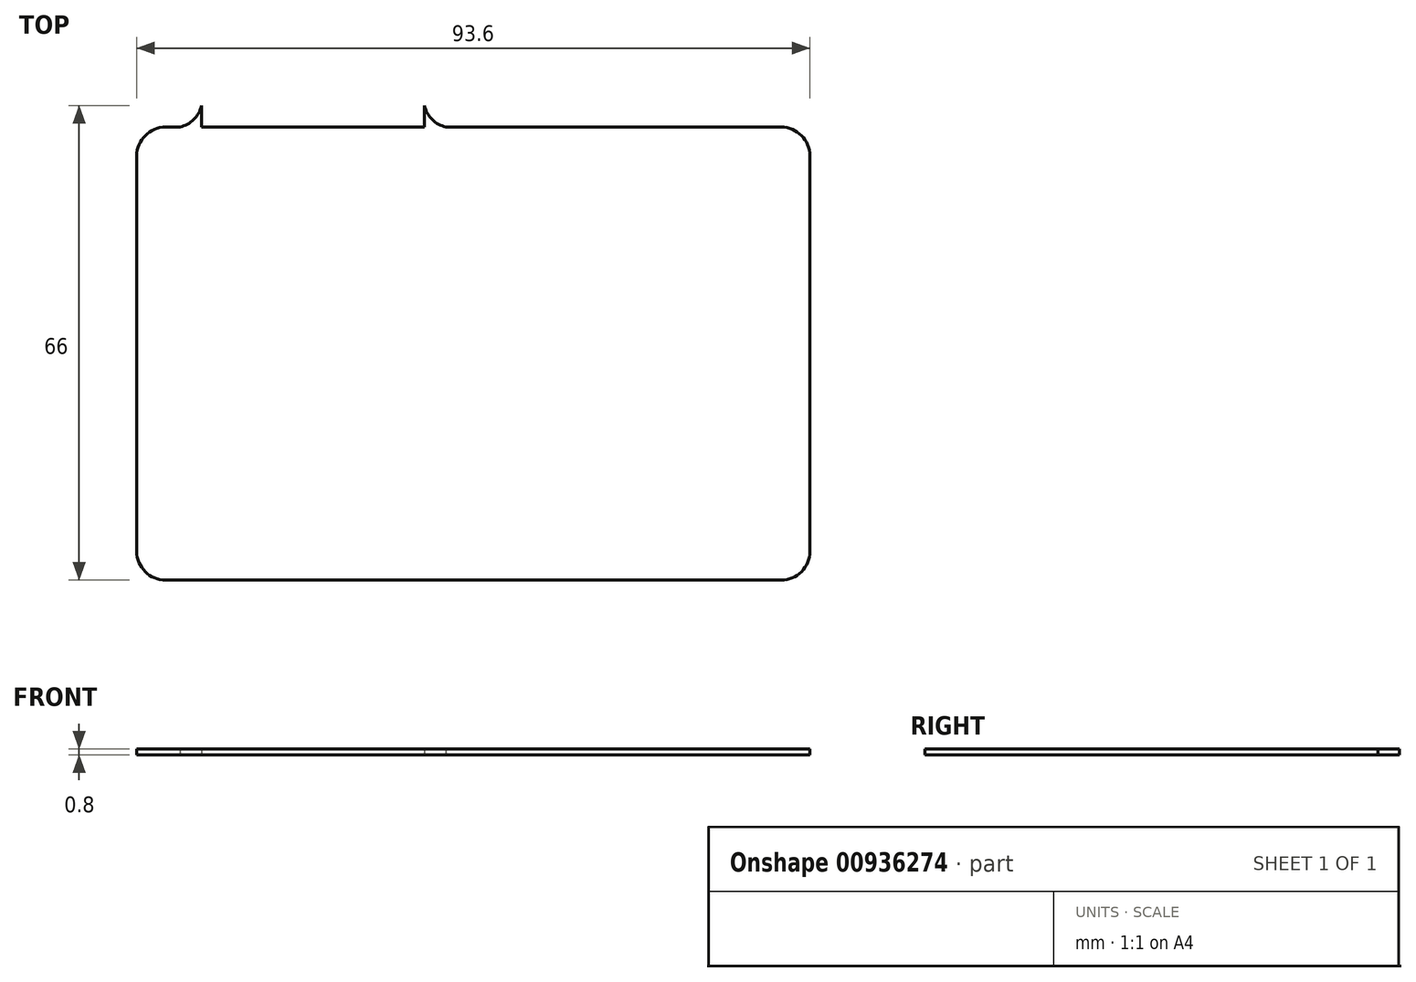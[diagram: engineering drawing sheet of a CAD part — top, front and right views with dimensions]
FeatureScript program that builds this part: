
annotation { "Feature Type Name" : "Feature", "Feature Type Description" : "" }
export const myFeature = defineFeature(function(context is Context, id is Id, definition is map)
    precondition{}
    {
        {
            var Q0;
            Q0=qCreatedBy(makeId("Top.planeOp"),FACE);
            var sketch = newSketch(context, id + "F0", { "sketchPlane" : qUnion([Q0])});
            skLineSegment(sketch, "E0.bottom", {"start": v(-34.53, 26.59) * mm, "end": v(51.07, 26.59) * mm});
            skLineSegment(sketch, "E0.top", {"start": v(-34.53, -36.41) * mm, "end": v(51.07, -36.41) * mm});
            skLineSegment(sketch, "E0.left", {"start": v(-38.53, 22.59) * mm, "end": v(-38.53, -32.41) * mm});
            skLineSegment(sketch, "E0.right", {"start": v(55.07, 22.59) * mm, "end": v(55.07, -32.41) * mm});
            skLineSegment(sketch, "E1.bottom", {"start": v(-29.53, 26.59) * mm, "end": v(1.47, 26.59) * mm});
            skLineSegment(sketch, "E1.top", {"start": v(-25.53, 35.59) * mm, "end": v(-2.53, 35.59) * mm});
            skLineSegment(sketch, "E1.left", {"start": v(-29.53, 26.59) * mm, "end": v(-29.53, 31.59) * mm});
            skLineSegment(sketch, "E1.right", {"start": v(1.47, 26.59) * mm, "end": v(1.47, 31.59) * mm});
            skPoint(sketch, "E2.visualSharp", {"position": v(-38.53, -36.41) * mm});
            skArc(sketch, "E2.filletArc", {"start": v(-38.53, -32.41) * mm, "mid": v(-37.36, -35.24) * mm, "end": v(-34.53, -36.41) * mm});
            skPoint(sketch, "E3.visualSharp", {"position": v(-38.53, 26.59) * mm});
            skArc(sketch, "E3.filletArc", {"start": v(-34.53, 26.59) * mm, "mid": v(-37.36, 25.42) * mm, "end": v(-38.53, 22.59) * mm});
            skPoint(sketch, "E4.visualSharp", {"position": v(55.07, 26.59) * mm});
            skArc(sketch, "E4.filletArc", {"start": v(55.07, 22.59) * mm, "mid": v(53.9, 25.42) * mm, "end": v(51.07, 26.59) * mm});
            skPoint(sketch, "E5.visualSharp", {"position": v(55.07, -36.41) * mm});
            skArc(sketch, "E5.filletArc", {"start": v(51.07, -36.41) * mm, "mid": v(53.9, -35.24) * mm, "end": v(55.07, -32.41) * mm});
            skPoint(sketch, "E6.visualSharp", {"position": v(1.47, 35.59) * mm});
            skArc(sketch, "E6.filletArc", {"start": v(1.47, 31.59) * mm, "mid": v(0.3, 34.42) * mm, "end": v(-2.53, 35.59) * mm});
            skPoint(sketch, "E7.visualSharp", {"position": v(-29.53, 35.59) * mm});
            skArc(sketch, "E7.filletArc", {"start": v(-25.53, 35.59) * mm, "mid": v(-28.36, 34.42) * mm, "end": v(-29.53, 31.59) * mm});
            skArc(sketch, "E8", {"start": v(1.47, 29.59) * mm, "mid": v(2.54, 27.66) * mm, "end": v(4.47, 26.59) * mm});
            skArc(sketch, "E9", {"start": v(-32.53, 26.59) * mm, "mid": v(-30.6, 27.66) * mm, "end": v(-29.53, 29.59) * mm});
            skSolve(sketch);
        }
        {
            var Q0;
            Q0=makeQuery(id+"F0.imprint","IMPRINT",FACE,{"disambiguationData":[TD([[makeQuery(id+"F0.imprint","IMPRINT",EDGE,{"derivedFrom":sQuery(id+"F0.wireOp",EDGE,"E0.top")}),1.0]])]});
            var Q1;
            {var subQ3=sQuery(id+"F0.wireOp",EDGE,"E1.bottom");Q1=makeQuery(id+"F0.imprint","IMPRINT",FACE,{"disambiguationData":[TD([[makeQuery(id+"F0.imprint","IMPRINT",EDGE,{"derivedFrom":subQ3}),1.0]])]});}
            var Q2;
            {var subQ3=sQuery(id+"F0.wireOp",EDGE,"E9");Q2=makeQuery(id+"F0.imprint","IMPRINT",FACE,{"disambiguationData":[TD([[makeQuery(id+"F0.imprint","IMPRINT",EDGE,{"derivedFrom":subQ3}),-1.0]])]});}
            var Q3;
            {var subQ3=sQuery(id+"F0.wireOp",EDGE,"E8");Q3=makeQuery(id+"F0.imprint","IMPRINT",FACE,{"disambiguationData":[TD([[makeQuery(id+"F0.imprint","IMPRINT",EDGE,{"derivedFrom":subQ3}),-1.0]])]});}
            extrude(context, id + "F1", {"entities" : qUnion([Q0, Q1, Q2, Q3]), "depth" : 0.8 * mm, "offsetDistance" : 25 * mm});
        }
    });
